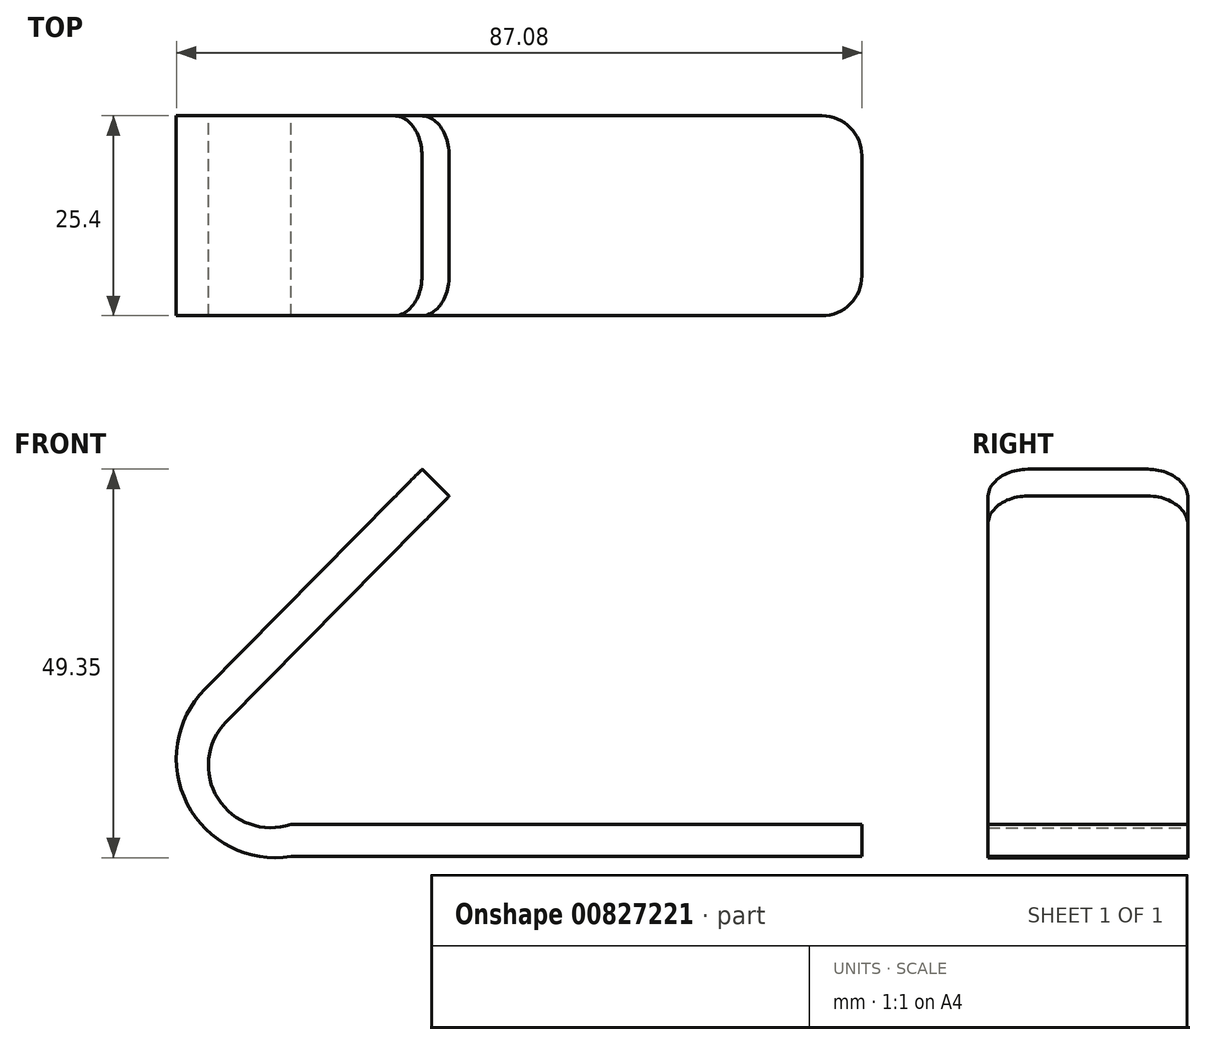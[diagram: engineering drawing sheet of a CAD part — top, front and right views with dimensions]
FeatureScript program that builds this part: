
annotation { "Feature Type Name" : "Feature", "Feature Type Description" : "" }
export const myFeature = defineFeature(function(context is Context, id is Id, definition is map)
    precondition{}
    {
        {
            var Q0;
            Q0=qCreatedBy(makeId("Front.planeOp"),FACE);
            var sketch = newSketch(context, id + "F0", { "sketchPlane" : qUnion([Q0])});
            skLineSegment(sketch, "E0", {"start": v(0, 31.45) * mm, "end": v(-28.32, 2.77) * mm});
            skArc(sketch, "E1", {"start": v(-28.32, 2.77) * mm, "mid": v(-29.38, -6.98) * mm, "end": v(-20.12, -10.24) * mm});
            skLineSegment(sketch, "E2", {"start": v(-20.12, -10.24) * mm, "end": v(52.42, -10.24) * mm});
            skLineSegment(sketch, "E3", {"start": v(52.42, -10.24) * mm, "end": v(52.42, -14.34) * mm});
            skLineSegment(sketch, "E4", {"start": v(52.42, -14.34) * mm, "end": v(-20.12, -14.34) * mm});
            skLineSegment(sketch, "E5", {"start": v(0, 31.45) * mm, "end": v(-3.46, 34.86) * mm});
            skLineSegment(sketch, "E6", {"start": v(-3.46, 34.86) * mm, "end": v(-31.03, 6.93) * mm});
            skArc(sketch, "E7", {"start": v(-31.03, 6.93) * mm, "mid": v(-33.28, -7.65) * mm, "end": v(-20.12, -14.34) * mm});
            skSolve(sketch);
        }
        {
            var Q0;
            Q0 = qSketchRegion(id + "F0", true);
            extrude(context, id + "F1", {"entities" : qUnion([Q0]), "depth" : 25.4 * mm, "offsetDistance" : 25.4 * mm});
        }
        {
            var Q0;
            Q0=makeQuery(id+"F1.opExtrude","CAP_EDGE",EDGE,{"disambiguationData":[OSD([sQuery(id+"F0.wireOp",EDGE,"E5")])],"isStart":false});
            var Q1;
            Q1=makeQuery(id+"F1.opExtrude","CAP_EDGE",EDGE,{"disambiguationData":[OSD([sQuery(id+"F0.wireOp",EDGE,"E5")])],"isStart":true});
            var Q2;
            Q2=makeQuery(id+"F1.opExtrude","CAP_EDGE",EDGE,{"disambiguationData":[OSD([sQuery(id+"F0.wireOp",EDGE,"E3")])],"isStart":false});
            var Q3;
            Q3=makeQuery(id+"F1.opExtrude","CAP_EDGE",EDGE,{"disambiguationData":[OSD([sQuery(id+"F0.wireOp",EDGE,"E3")])],"isStart":true});
            fillet(context, id + "F2", {"entities" : qUnion([Q0, Q1, Q2, Q3]), "radius" : 5.08 * mm, "tangentPropagation" : true, "allowEdgeOverflow" : false});
        }
    });
